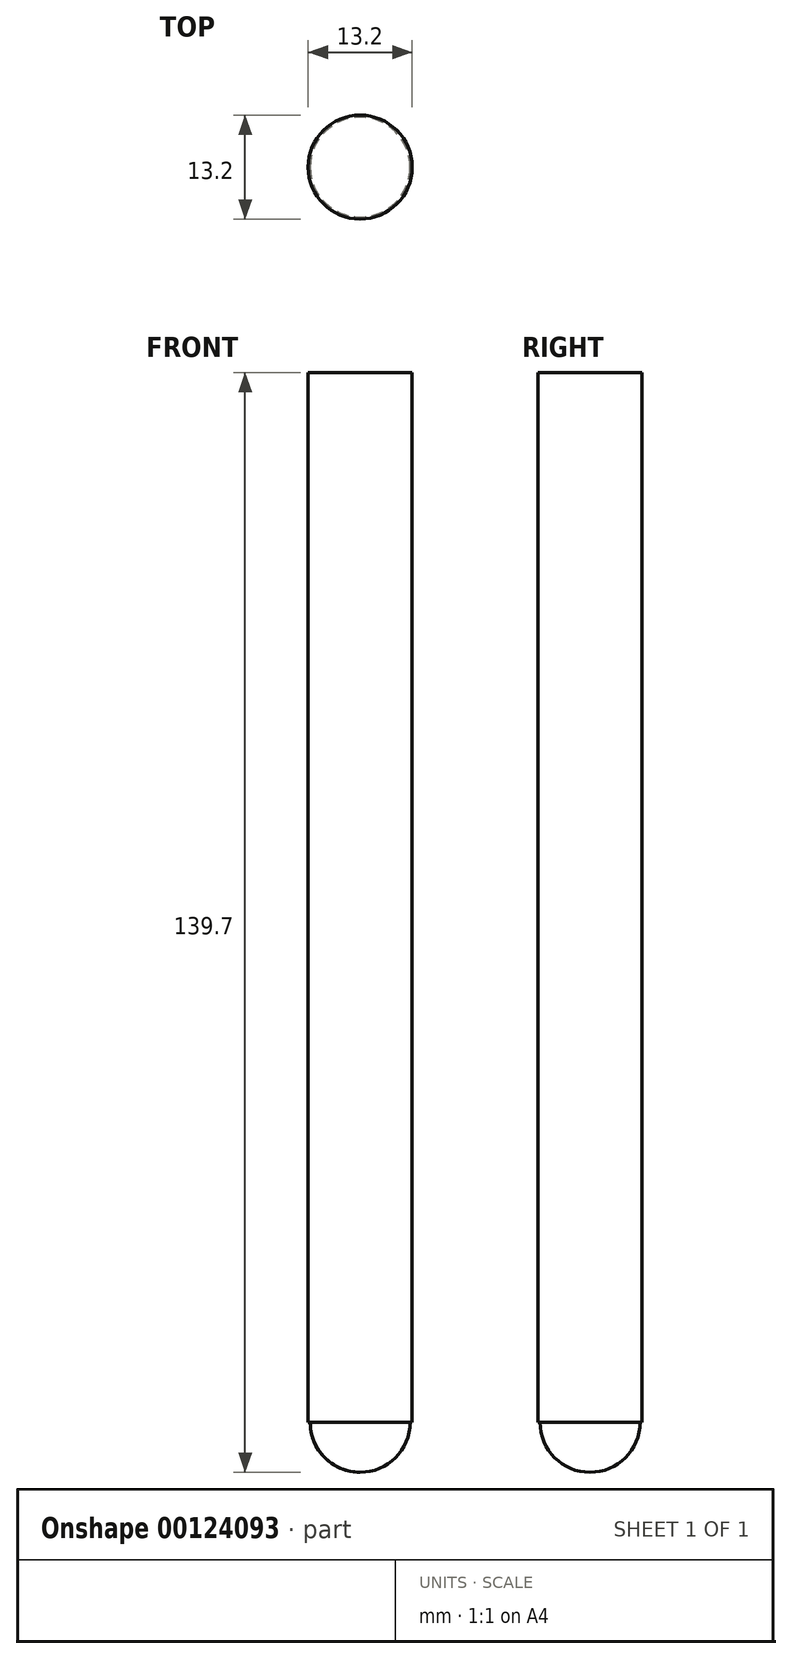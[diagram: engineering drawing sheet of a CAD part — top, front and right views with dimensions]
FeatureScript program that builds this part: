
annotation { "Feature Type Name" : "Feature", "Feature Type Description" : "" }
export const myFeature = defineFeature(function(context is Context, id is Id, definition is map)
    precondition{}
    {
        {
            var Q0;
            Q0=qCreatedBy(makeId("Top.planeOp"),FACE);
            var sketch = newSketch(context, id + "F0", { "sketchPlane" : qUnion([Q0])});
            skCircle(sketch, "E0", {"center": v(0, 0) * mm, "radius": 6.6 * mm});
            skSolve(sketch);
        }
        {
            var Q0;
            Q0=makeQuery(id+"F0.imprint","IMPRINT",FACE,{"disambiguationData":[TD([[makeQuery(id+"F0.imprint","IMPRINT",EDGE,{"derivedFrom":sQuery(id+"F0.wireOp",EDGE,"E0")}),1.0]])]});
            extrude(context, id + "F1", {"entities" : qUnion([Q0]), "depth" : 139.7 * mm});
        }
        {
            var Q0;
            Q0=qCreatedBy(makeId("Front.planeOp"),FACE);
            var sketch = newSketch(context, id + "F2", { "sketchPlane" : qUnion([Q0])});
            skLineSegment(sketch, "E1", {"start": v(0, 0) * mm, "end": v(0, 18.3) * mm, "construction": true});
            skLineSegment(sketch, "E2", {"start": v(0, 0) * mm, "end": v(-43.42, 0) * mm, "construction": true});
            skArc(sketch, "E3", {"start": v(0, 0) * mm, "mid": v(4.5, 1.86) * mm, "end": v(6.35, 6.35) * mm});
            skLineSegment(sketch, "E4", {"start": v(6.35, 6.35) * mm, "end": v(17.5, 6.35) * mm});
            skLineSegment(sketch, "E5", {"start": v(17.5, 6.35) * mm, "end": v(17.5, -9.46) * mm});
            skLineSegment(sketch, "E6", {"start": v(17.5, -9.46) * mm, "end": v(0, -9.46) * mm});
            skLineSegment(sketch, "E7", {"start": v(0, -9.46) * mm, "end": v(0, 0) * mm});
            skLineSegment(sketch, "E8", {"start": v(6.35, 6.35) * mm, "end": v(6.35, 32.26) * mm, "construction": true});
            skSolve(sketch);
        }
        {
            var Q0;
            Q0 = qSketchRegion(id + "F2", true);
            var Q1;
            Q1=sQuery(id+"F2.wireOp",EDGE,"E1");
            revolve(context, id + "F3", {"operationType" : NewBodyOperationType.REMOVE, "entities" : qUnion([Q0]), "axis" : qUnion([Q1]), "revolveType" : RevolveType.FULL, "oppositeDirection" : true});
        }
    });
